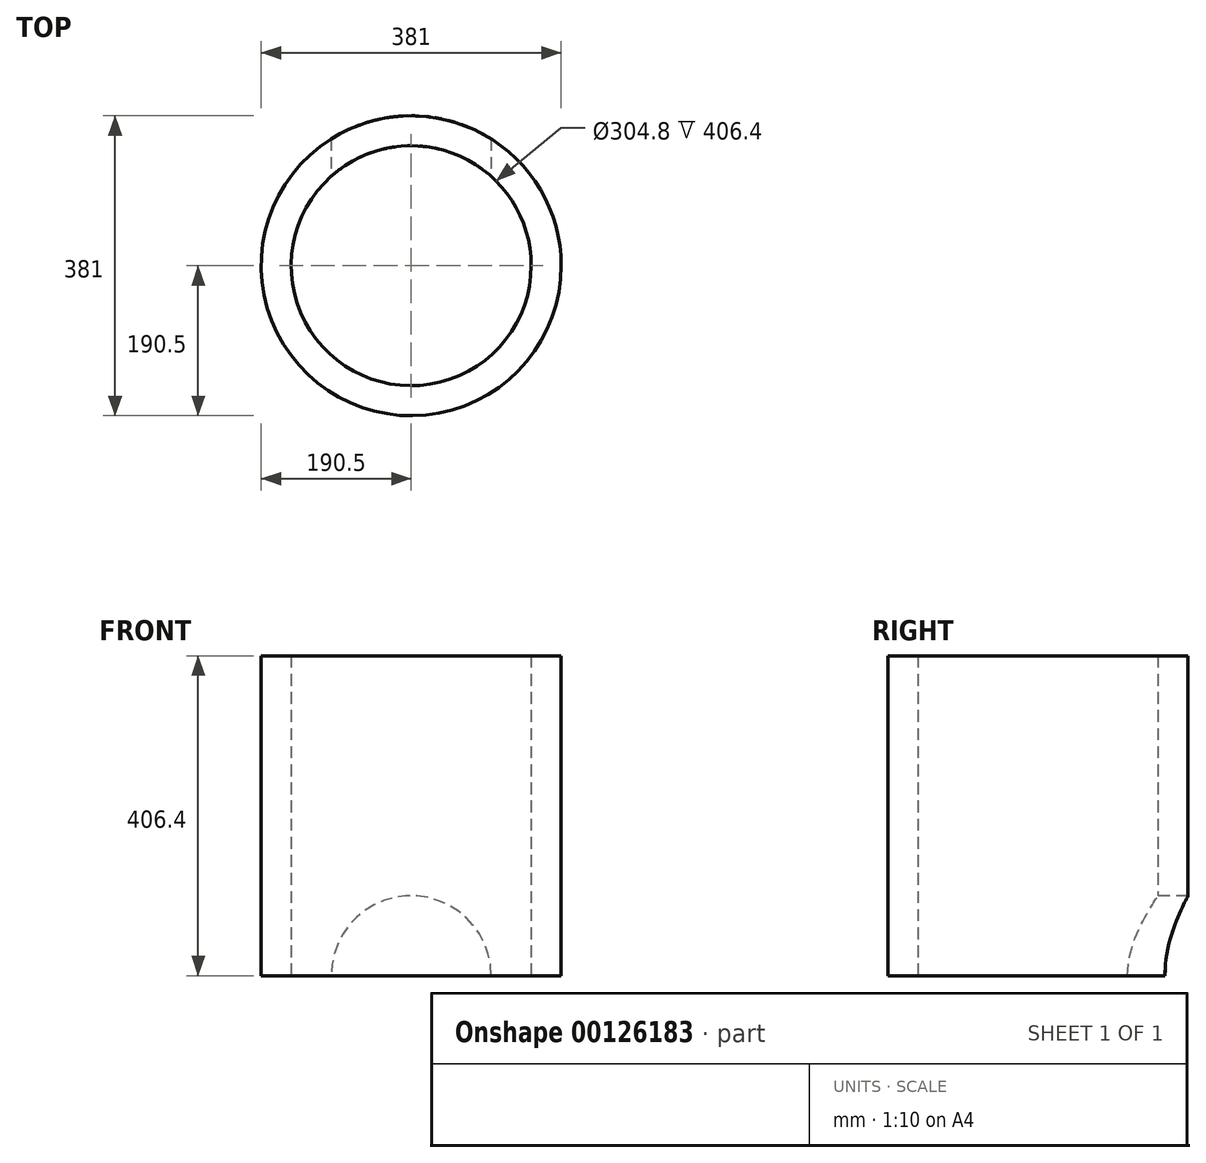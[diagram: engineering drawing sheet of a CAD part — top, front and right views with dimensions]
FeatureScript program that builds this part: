
annotation { "Feature Type Name" : "Feature", "Feature Type Description" : "" }
export const myFeature = defineFeature(function(context is Context, id is Id, definition is map)
    precondition{}
    {
        {
            var Q0;
            Q0=qCreatedBy(makeId("Top.planeOp"),FACE);
            var sketch = newSketch(context, id + "F0", { "sketchPlane" : qUnion([Q0])});
            skCircle(sketch, "E0", {"center": v(0, 0) * mm, "radius": 190.5 * mm});
            skCircle(sketch, "E1", {"center": v(0, 0) * mm, "radius": 152.4 * mm});
            skSolve(sketch);
        }
        {
            var Q0;
            Q0=makeQuery(id+"F0.imprint","IMPRINT",FACE,{"disambiguationData":[TD([[makeQuery(id+"F0.imprint","IMPRINT",EDGE,{"derivedFrom":sQuery(id+"F0.wireOp",EDGE,"E0")}),1.0]])]});
            extrude(context, id + "F1", {"entities" : qUnion([Q0]), "flatOperationType" : FlatOperationType.REMOVE, "offsetDistance" : 25.4 * mm, "depth" : 406.4 * mm, "domain" : OperationDomain.MODEL});
        }
        {
            var Q0;
            Q0=qCreatedBy(makeId("Front.planeOp"),FACE);
            var sketch = newSketch(context, id + "F2", { "sketchPlane" : qUnion([Q0])});
            skArc(sketch, "E2", {"start": v(101.6, 0) * mm, "mid": v(0, 101.6) * mm, "end": v(-101.6, 0) * mm});
            skLineSegment(sketch, "E3", {"start": v(-101.6, 0) * mm, "end": v(101.6, 0) * mm});
            skSolve(sketch);
        }
        {
            var Q0;
            Q0=makeQuery(id+"F2.imprint","IMPRINT",FACE,{"disambiguationData":[TD([[makeQuery(id+"F2.imprint","IMPRINT",EDGE,{"derivedFrom":sQuery(id+"F2.wireOp",EDGE,"E2")}),1.0]])]});
            extrude(context, id + "F3", {"entities" : qUnion([Q0]), "operationType" : NewBodyOperationType.REMOVE, "flatOperationType" : FlatOperationType.REMOVE, "oppositeDirection" : true, "offsetDistance" : 25.4 * mm, "depth" : 254 * mm, "domain" : OperationDomain.MODEL});
        }
    });
